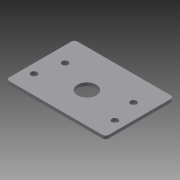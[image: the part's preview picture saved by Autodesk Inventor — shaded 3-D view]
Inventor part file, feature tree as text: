
AUTODESK INVENTOR PART (.ipt)
format: ipt  version: 2013 (Build 170138000, 138)  size: 105,984 bytes
history: native  units: in
note: dims shown in document units (in); Inventor stores cm internally (conversion verified against a paired STEP export)
features: sketch x3, hole x2, extrude x1
ambient origin geometry x8: Origin, YZ Plane, XZ Plane, XY Plane, X Axis, Y Axis, Z Axis, Center Point
bodies: Solid1 (feature_tree)
feature tree (6):
  extrude  "Extrusion1"  Depth=2.75in
  hole  "Hole1"  [1 undecoded]
  hole  "Hole2"  [1 undecoded]
  sketch  "Sketch1"  dims[d0=4.0in d1=2.75in]
  sketch  "Sketch2"  dims[d2=0.125in d3=0.0in d4=2.0in]
  sketch  "Sketch3"  dims[d5=1.5in d6=0.75in d7=0.75in d8=0.375in d9=0.25in d10=0.5635in d11=1.0in d12=0.8108in d13=0.125in d22=0.25in d23=0.75in d24=0.375in d25=0.25in d26=0.5635in d27=1.0in d28=0.8108in d29=2.0in d30=0.25in d33=1.0in d36=0.375in d37=0.375in d38=0.25in d39=0.5in d40=3.25in]
note: 2 required parameter values undecoded (feature->parameter linkage not recoverable at this tier; creation-order binding heuristic only, values carry confidence <= 0.55)
